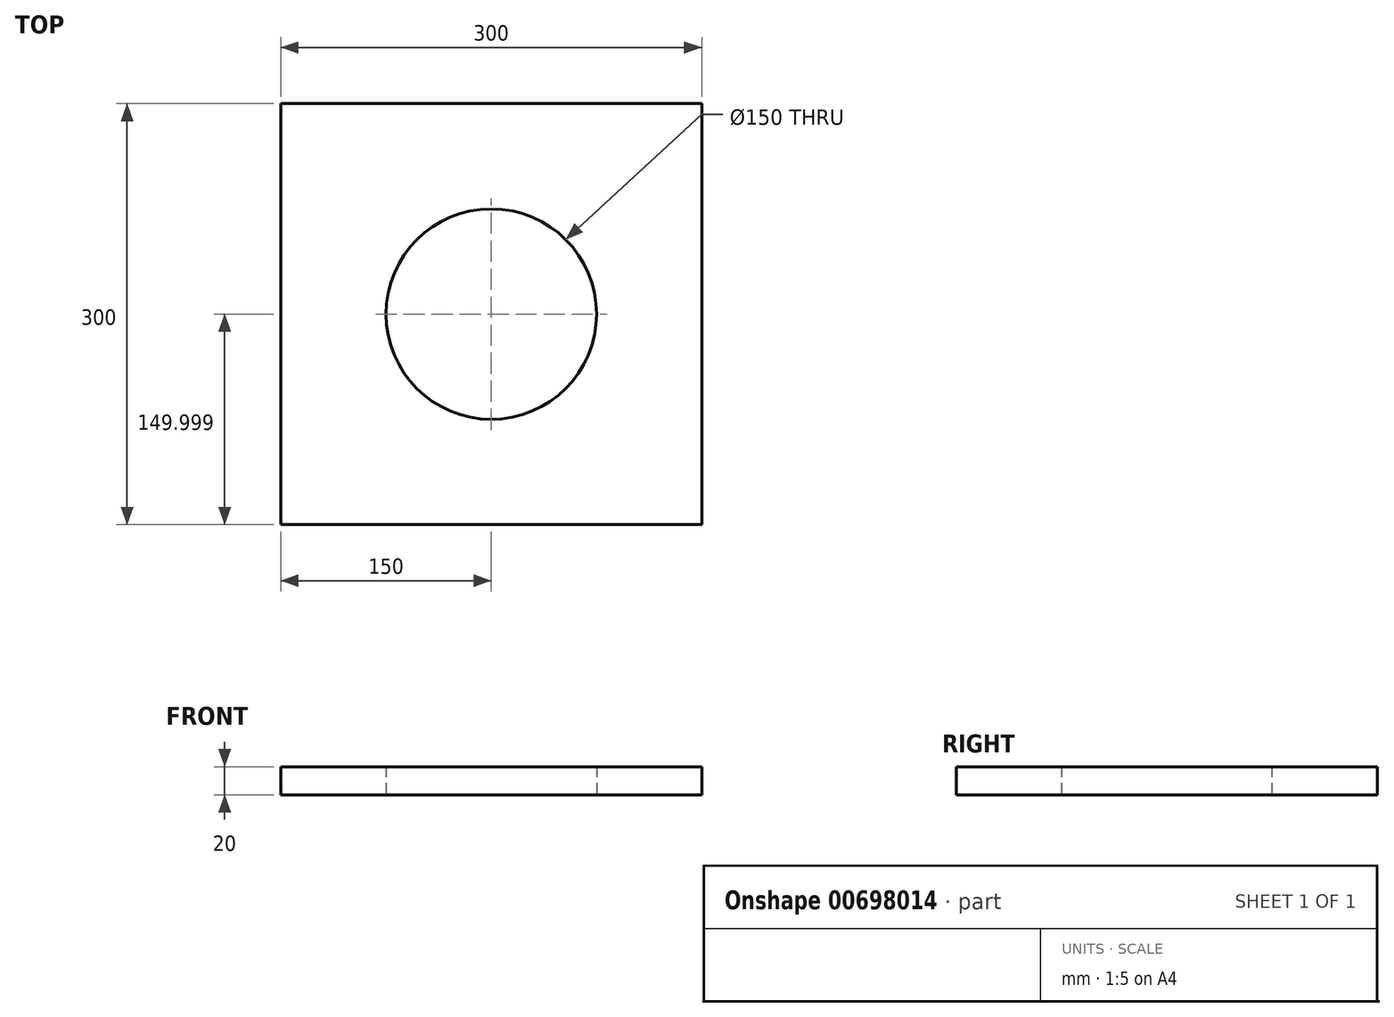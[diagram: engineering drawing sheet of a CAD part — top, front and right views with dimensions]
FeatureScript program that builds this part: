
annotation { "Feature Type Name" : "Feature", "Feature Type Description" : "" }
export const myFeature = defineFeature(function(context is Context, id is Id, definition is map)
    precondition{}
    {
        {
            var Q0;
            Q0=qCreatedBy(makeId("Top.planeOp"),FACE);
            var sketch = newSketch(context, id + "F0", { "sketchPlane" : qUnion([Q0])});
            skLineSegment(sketch, "E0.bottom", {"start": v(0, -28.08) * mm, "end": v(-300, -28.08) * mm});
            skLineSegment(sketch, "E0.top", {"start": v(0, 271.92) * mm, "end": v(-300, 271.92) * mm});
            skLineSegment(sketch, "E0.left", {"start": v(0, -28.08) * mm, "end": v(0, 271.92) * mm});
            skLineSegment(sketch, "E0.right", {"start": v(-300, -28.08) * mm, "end": v(-300, 271.92) * mm});
            skSolve(sketch);
        }
        {
            var Q0;
            Q0=makeQuery(id+"F0.imprint","IMPRINT",FACE,{"disambiguationData":[TD([[makeQuery(id+"F0.imprint","IMPRINT",EDGE,{"derivedFrom":sQuery(id+"F0.wireOp",EDGE,"E0.bottom")}),-1.0]])]});
            var sketch = newSketch(context, id + "F1", { "sketchPlane" : qUnion([Q0])});
            skCircle(sketch, "E1", {"center": v(-150, 121.92) * mm, "radius": 75 * mm});
            skSolve(sketch);
        }
        {
            var Q0;
            Q0=makeQuery(id+"F0.imprint","IMPRINT",FACE,{"disambiguationData":[TD([[makeQuery(id+"F0.imprint","IMPRINT",EDGE,{"derivedFrom":sQuery(id+"F0.wireOp",EDGE,"E0.bottom")}),-1.0]])]});
            extrude(context, id + "F2", {"entities" : qUnion([Q0]), "depth" : 20 * mm, "offsetDistance" : 25 * mm});
        }
        {
            var Q0;
            Q0=makeQuery(id+"F1.imprint","IMPRINT",FACE,{"disambiguationData":[TD([[makeQuery(id+"F1.imprint","IMPRINT",EDGE,{"derivedFrom":sQuery(id+"F1.wireOp",EDGE,"E1")}),1.0]])]});
            extrude(context, id + "F3", {"entities" : qUnion([Q0]), "operationType" : NewBodyOperationType.REMOVE, "endBound" : BoundingType.THROUGH_ALL, "depth" : 25 * mm, "offsetDistance" : 25 * mm});
        }
    });
